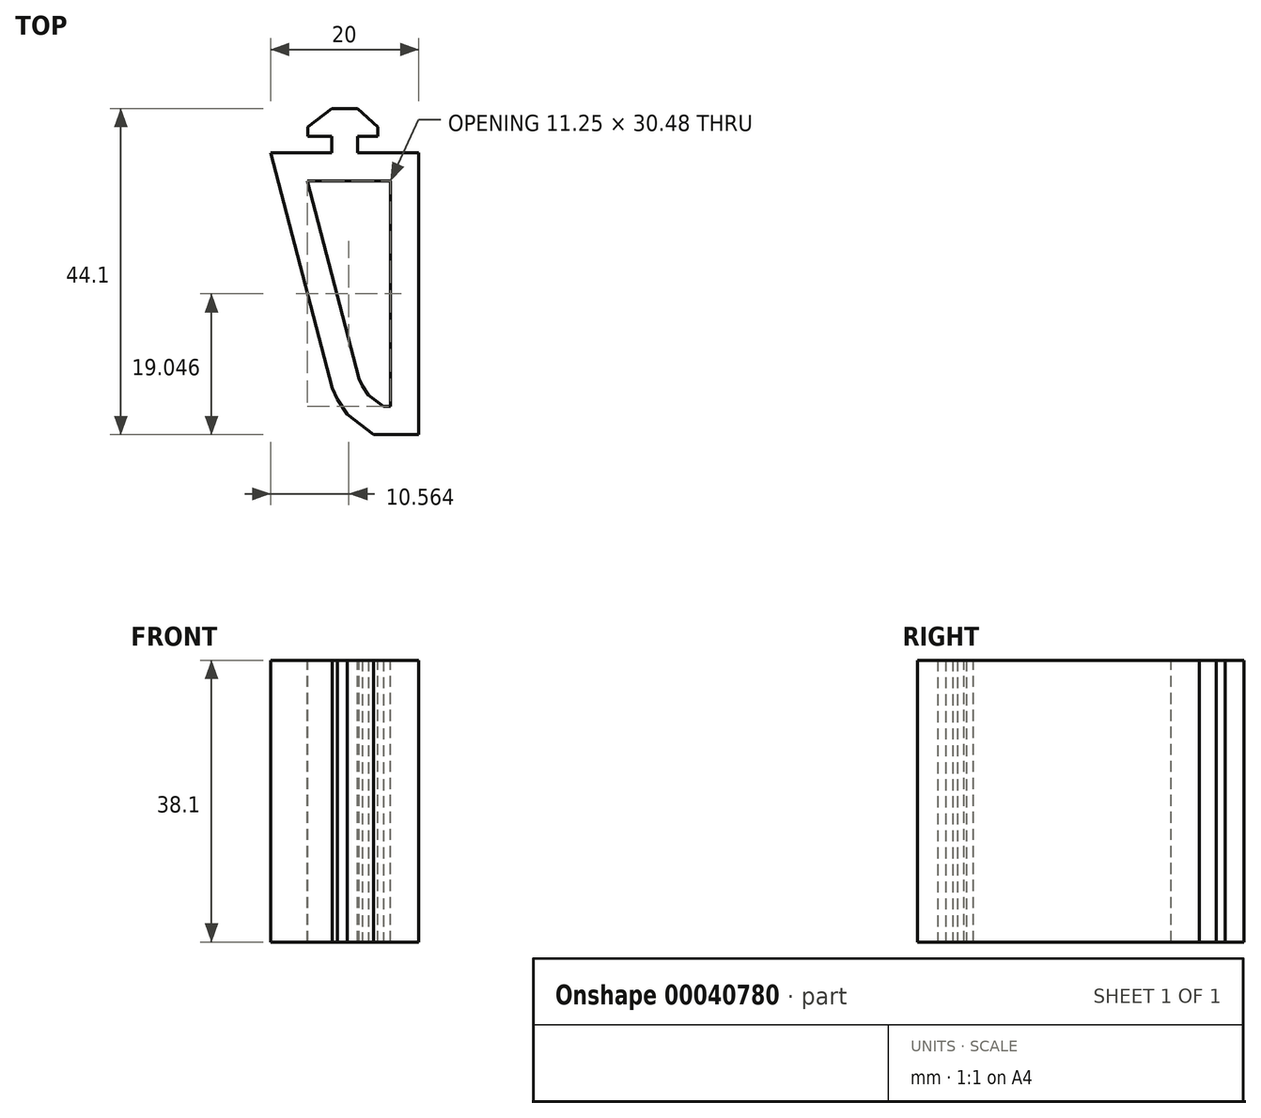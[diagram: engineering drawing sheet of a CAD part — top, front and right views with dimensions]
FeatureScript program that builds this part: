
annotation { "Feature Type Name" : "Feature", "Feature Type Description" : "" }
export const myFeature = defineFeature(function(context is Context, id is Id, definition is map)
    precondition{}
    {
        {
            var Q0;
            Q0=qCreatedBy(makeId("Top.planeOp"),FACE);
            var sketch = newSketch(context, id + "F0", { "sketchPlane" : qUnion([Q0])});
            skLineSegment(sketch, "E0.top", {"start": v(48.7, -17.12) * mm, "end": v(52.2, -17.12) * mm});
            skLineSegment(sketch, "E0.left", {"start": v(48.7, -19.37) * mm, "end": v(48.7, -17.12) * mm});
            skLineSegment(sketch, "E0.right", {"start": v(52.2, -19.37) * mm, "end": v(52.2, -17.12) * mm});
            skLineSegment(sketch, "E1.bottom", {"start": v(45.45, -17.12) * mm, "end": v(54.95, -17.12) * mm});
            skLineSegment(sketch, "E1.top", {"start": v(45.45, -15.87) * mm, "end": v(54.95, -15.87) * mm});
            skLineSegment(sketch, "E1.left", {"start": v(45.45, -17.12) * mm, "end": v(45.45, -15.87) * mm});
            skLineSegment(sketch, "E1.right", {"start": v(54.95, -17.12) * mm, "end": v(54.95, -15.87) * mm});
            skLineSegment(sketch, "E2", {"start": v(45.45, -15.87) * mm, "end": v(48.7, -13.37) * mm});
            skPoint(sketch, "E2.endSnap0", {"position": v(48.7, -18.25) * mm});
            skLineSegment(sketch, "E3", {"start": v(48.7, -13.37) * mm, "end": v(52.2, -13.37) * mm});
            skLineSegment(sketch, "E4", {"start": v(52.2, -13.37) * mm, "end": v(54.95, -15.87) * mm});
            skLineSegment(sketch, "E5", {"start": v(48.7, -19.37) * mm, "end": v(52.2, -19.37) * mm});
            skLineSegment(sketch, "E6.bottom", {"start": v(40.45, -19.37) * mm, "end": v(60.45, -19.37) * mm});
            skLineSegment(sketch, "E6.top", {"start": v(40.45, -57.47) * mm, "end": v(60.45, -57.47) * mm});
            skLineSegment(sketch, "E6.left", {"start": v(40.45, -19.37) * mm, "end": v(40.45, -57.47) * mm});
            skLineSegment(sketch, "E6.right", {"start": v(60.45, -19.37) * mm, "end": v(60.45, -57.47) * mm});
            skLineSegment(sketch, "E7", {"start": v(50.45, -19.37) * mm, "end": v(50.45, -24.58) * mm, "construction": true});
            skLineSegment(sketch, "E8", {"start": v(50.45, -57.47) * mm, "end": v(40.45, -19.37) * mm});
            skSolve(sketch);
        }
        {
            var Q0;
            {var subQ0=sQuery(id+"F0.wireOp",EDGE,"E6.right");Q0=makeQuery(id+"F0.imprint","IMPRINT",FACE,{"disambiguationData":[TD([[makeQuery(id+"F0.imprint","IMPRINT",EDGE,{"derivedFrom":subQ0}),-1.0]])]});}
            extrude(context, id + "F1", {"entities" : qUnion([Q0]), "oppositeDirection" : true, "depth" : 38.1 * mm});
        }
        {
            var Q0;
            Q0=makeQuery(id+"F1.opExtrude","SWEPT_EDGE",EDGE,{"disambiguationData":[OSD([sQuery(id+"F0.wireOp",EDGE,"E6.top"),sQuery(id+"F0.wireOp",EDGE,"E8")])]});
            chamfer(context, id + "F2", {"entities" : qUnion([Q0]), "width" : 5.08 * mm, "tangentPropagation" : true});
        }
        {
            var Q0;
            {var subQ0=sQuery(id+"F0.wireOp",EDGE,"E8");Q0=makeQuery(id+"F2.opChamfer","BLEND_EDGE",EDGE,{"blendedFrom":[makeQuery(id+"F1.opExtrude","SWEPT_EDGE",EDGE,{"disambiguationData":[OSD([sQuery(id+"F0.wireOp",EDGE,"E6.top"),subQ0])]}),makeQuery(id+"F1.opExtrude","SWEPT_FACE",FACE,{"disambiguationData":[OSD([subQ0])]})],"blendedInto":[makeQuery(id+"F1.opExtrude","SWEPT_FACE",FACE,{"disambiguationData":[OSD([subQ0])]})]});}
            chamfer(context, id + "F3", {"entities" : qUnion([Q0]), "width" : 5.08 * mm, "tangentPropagation" : true});
        }
        {
            var Q0;
            {var subQ0=sQuery(id+"F0.wireOp",EDGE,"E8");var subQ1=makeQuery(id+"F1.opExtrude","SWEPT_FACE",FACE,{"disambiguationData":[OSD([subQ0])]});Q0=makeQuery(id+"F3.opChamfer","BLEND_EDGE",EDGE,{"blendedFrom":[makeQuery(id+"F2.opChamfer","BLEND_EDGE",EDGE,{"blendedFrom":[makeQuery(id+"F1.opExtrude","SWEPT_EDGE",EDGE,{"disambiguationData":[OSD([sQuery(id+"F0.wireOp",EDGE,"E6.top"),subQ0])]}),subQ1],"blendedInto":[subQ1]}),subQ1],"blendedInto":[subQ1]});}
            chamfer(context, id + "F4", {"entities" : qUnion([Q0]), "width" : 5.08 * mm, "tangentPropagation" : true});
        }
        {
            var Q0;
            Q0=makeQuery(id+"F1.opExtrude","CAP_FACE",FACE,{"disambiguationData":[OSD([sQuery(id+"F0.wireOp",EDGE,"E6.bottom"),sQuery(id+"F0.wireOp",EDGE,"E6.top"),sQuery(id+"F0.wireOp",EDGE,"E6.right"),sQuery(id+"F0.wireOp",EDGE,"E8")])],"isStart":false});
            var Q1;
            Q1=makeQuery(id+"F1.opExtrude","SWEPT_BODY",BODY,{"disambiguationData":[OSD([sQuery(id+"F0.wireOp",EDGE,"E6.bottom"),sQuery(id+"F0.wireOp",EDGE,"E6.top"),sQuery(id+"F0.wireOp",EDGE,"E6.right"),sQuery(id+"F0.wireOp",EDGE,"E8")])]});
            shell(context, id + "F5", {"entities" : qUnion([Q0]), "parts" : qUnion([Q1]), "thickness" : 3.8 * mm});
        }
        {
            var Q0;
            Q0=makeQuery(id+"F5.opShell","OFFSET_FACE",FACE,{"disambiguationData":[OSD([sQuery(id+"F0.wireOp",EDGE,"E6.bottom"),sQuery(id+"F0.wireOp",EDGE,"E6.top"),sQuery(id+"F0.wireOp",EDGE,"E6.right"),sQuery(id+"F0.wireOp",EDGE,"E8")])]});
            extrude(context, id + "F6", {"entities" : qUnion([Q0]), "operationType" : NewBodyOperationType.REMOVE, "oppositeDirection" : true, "depth" : 25.4 * mm});
        }
        {
            var Q0;
            {var subQ0=sQuery(id+"F0.wireOp",EDGE,"E0.left");Q0=makeQuery(id+"F0.imprint","IMPRINT",FACE,{"disambiguationData":[TD([[makeQuery(id+"F0.imprint","IMPRINT",EDGE,{"derivedFrom":subQ0}),-1.0]])]});}
            var Q1;
            Q1=makeQuery(id+"F0.imprint","IMPRINT",FACE,{"disambiguationData":[TD([[makeQuery(id+"F0.imprint","IMPRINT",EDGE,{"derivedFrom":sQuery(id+"F0.wireOp",EDGE,"E1.top")}),-1.0]])]});
            var Q2;
            Q2=makeQuery(id+"F0.imprint","IMPRINT",FACE,{"disambiguationData":[TD([[makeQuery(id+"F0.imprint","IMPRINT",EDGE,{"derivedFrom":sQuery(id+"F0.wireOp",EDGE,"E1.top")}),1.0]])]});
            extrude(context, id + "F7", {"entities" : qUnion([Q0, Q1, Q2]), "operationType" : NewBodyOperationType.ADD, "oppositeDirection" : true, "depth" : 38.1 * mm});
        }
    });
